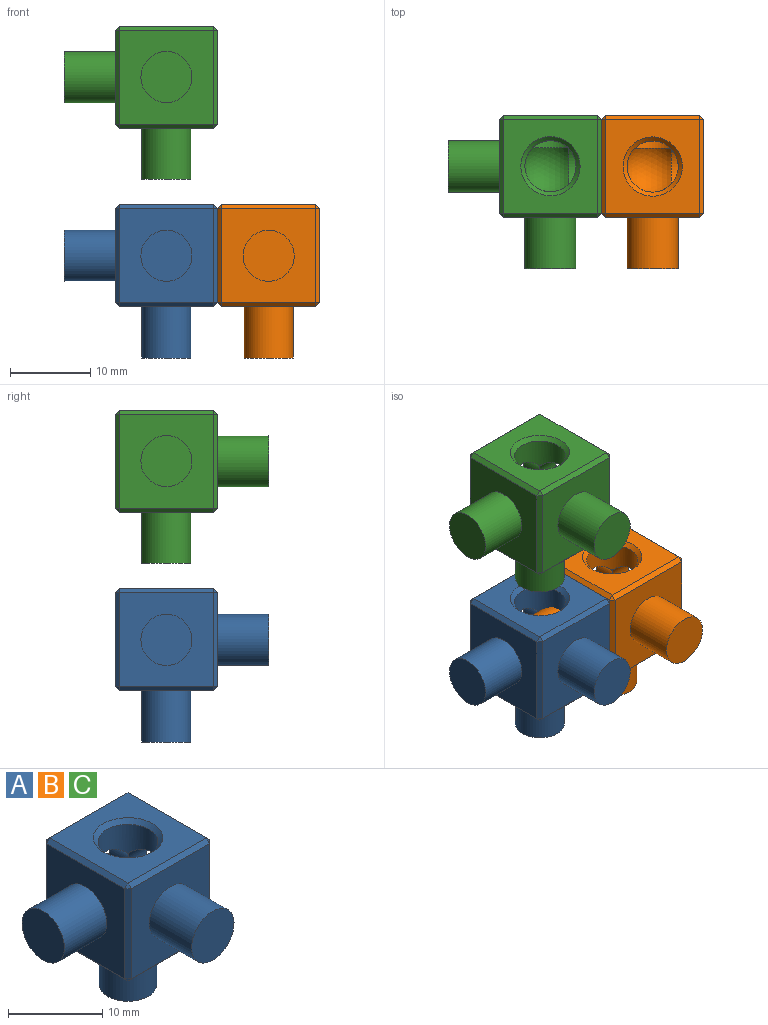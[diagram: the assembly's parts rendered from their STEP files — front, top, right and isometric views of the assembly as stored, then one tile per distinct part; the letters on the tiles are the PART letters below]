
ASSEMBLY  parts=3 mates=2
PART A: 40 faces, bbox 19.1x19.1x19.1 mm
  f0: cylinder r=3.05mm len=6.1mm, axis (1,0,0), area 63mm2, adj f7,f14,f15,f16,f38
  f1: plane 11.68x11.68mm, normal (0,-1,0), area 104.8mm2, adj f12,f20,f21,f30,f31
  f2: plane 11.68x11.68mm, normal (1,0,0), area 96.8mm2, adj f17,f21,f22,f23,f38
  f3: plane 11.68x11.68mm, normal (0,1,0), area 96.8mm2, adj f23,f24,f32,f33,f37
  f4: plane 11.68x11.68mm, normal (-1,0,0), area 104.8mm2, adj f10,f25,f30,f33,f36
  f5: plane 11.68x11.68mm, normal (0,0,1), area 93.9mm2, adj f17,f20,f24,f25,f39
  f6: plane 11.68x11.68mm, normal (0,0,-1), area 107.3mm2, adj f8,f22,f31,f32,f36
  f7: cylinder r=3.17mm len=6.35mm, axis (0,0,1), area 68.4mm2, adj f0,f14,f15,f16,f39
  f8: cylinder r=3.05mm len=6.35mm, axis (0,0,1), area 121.6mm2, adj f6,f9
  f9: plane 6.1x6.1mm, normal (0,0,-1), area 29.2mm2, adj f8
  f10: cylinder r=3.17mm len=6.35mm, axis (1,0,0), area 126.7mm2, adj f4,f11
  f11: plane 6.35x6.35mm, normal (-1,0,0), area 31.7mm2, adj f10
  f12: cylinder r=3.17mm len=6.35mm, axis (0,1,0), area 126.7mm2, adj f1,f13
  f13: plane 6.35x6.35mm, normal (0,-1,0), area 31.7mm2, adj f12
  f14: cylinder r=3.05mm len=6.1mm, axis (0,1,0), area 63mm2, adj f0,f7,f15,f16,f37
  f15: sphere r=3.81mm, area 79.9mm2, adj f0,f7,f14
  f16: sphere r=3.81mm, area 0mm2, adj f0,f7,f14
  f17: plane 11.68x0.51mm, normal (0.71,0,0.71), area 8.4mm2, adj f2,f5,f18,f19
  f18: plane 0.51x0.51mm, normal (0.58,-0.58,0.58), area 0.2mm2, adj f17,f20,f21
  f19: plane 0.51x0.51mm, normal (0.58,0.58,0.58), area 0.2mm2, adj f17,f23,f24
  f20: plane 11.68x0.51mm, normal (0,-0.71,0.71), area 8.4mm2, adj f1,f5,f18,f26
  f21: plane 11.68x0.51mm, normal (0.71,-0.71,0), area 8.4mm2, adj f1,f2,f18,f27
  f22: plane 11.68x0.51mm, normal (0.71,0,-0.71), area 8.4mm2, adj f2,f6,f27,f28
  f23: plane 11.68x0.51mm, normal (0.71,0.71,0), area 8.4mm2, adj f2,f3,f19,f28
  f24: plane 11.68x0.51mm, normal (0,0.71,0.71), area 8.4mm2, adj f3,f5,f19,f29
  f25: plane 11.68x0.51mm, normal (-0.71,0,0.71), area 8.4mm2, adj f4,f5,f26,f29
  f26: plane 0.51x0.51mm, normal (-0.58,-0.58,0.58), area 0.2mm2, adj f20,f25,f30
  f27: plane 0.51x0.51mm, normal (0.58,-0.58,-0.58), area 0.2mm2, adj f21,f22,f31
  f28: plane 0.51x0.51mm, normal (0.58,0.58,-0.58), area 0.2mm2, adj f22,f23,f32
  f29: plane 0.51x0.51mm, normal (-0.58,0.58,0.58), area 0.2mm2, adj f24,f25,f33
  f30: plane 11.68x0.51mm, normal (-0.71,-0.71,0), area 8.4mm2, adj f1,f4,f26,f34
  f31: plane 11.68x0.51mm, normal (0,-0.71,-0.71), area 8.4mm2, adj f1,f6,f27,f34
  f32: plane 11.68x0.51mm, normal (0,0.71,-0.71), area 8.4mm2, adj f3,f6,f28,f35
  f33: plane 11.68x0.51mm, normal (-0.71,0.71,0), area 8.4mm2, adj f3,f4,f29,f35
  f34: plane 0.51x0.51mm, normal (-0.58,-0.58,-0.58), area 0.2mm2, adj f30,f31,f36
  f35: plane 0.51x0.51mm, normal (-0.58,0.58,-0.58), area 0.2mm2, adj f32,f33,f36
  f36: plane 11.68x0.51mm, normal (-0.71,0,-0.71), area 8.4mm2, adj f4,f6,f34,f35
  f37: cone r=3.05mm half-angle=45deg, axis (0,1,0), area 14.9mm2, adj f3,f14
  f38: cone r=3.05mm half-angle=45deg, axis (1,0,0), area 14.9mm2, adj f0,f2
  f39: cone r=3.17mm half-angle=45deg, axis (0,0,1), area 15.5mm2, adj f5,f7
PART B: same geometry as A
PART C: same geometry as A
PLACE A t=(-5.67,-1.76,1.77)mm
PLACE B t=(7.03,-1.76,1.77)mm
PLACE C t=(-5.67,-1.76,23.98)mm
MATE slider B.f0 <-> A.f0  axis (1,0,0) through (-8.85,4.59,8.12)mm
MATE slider A.f7 <-> C.f7  axis (0,0,1) through (-12.02,4.59,13.96)mm
